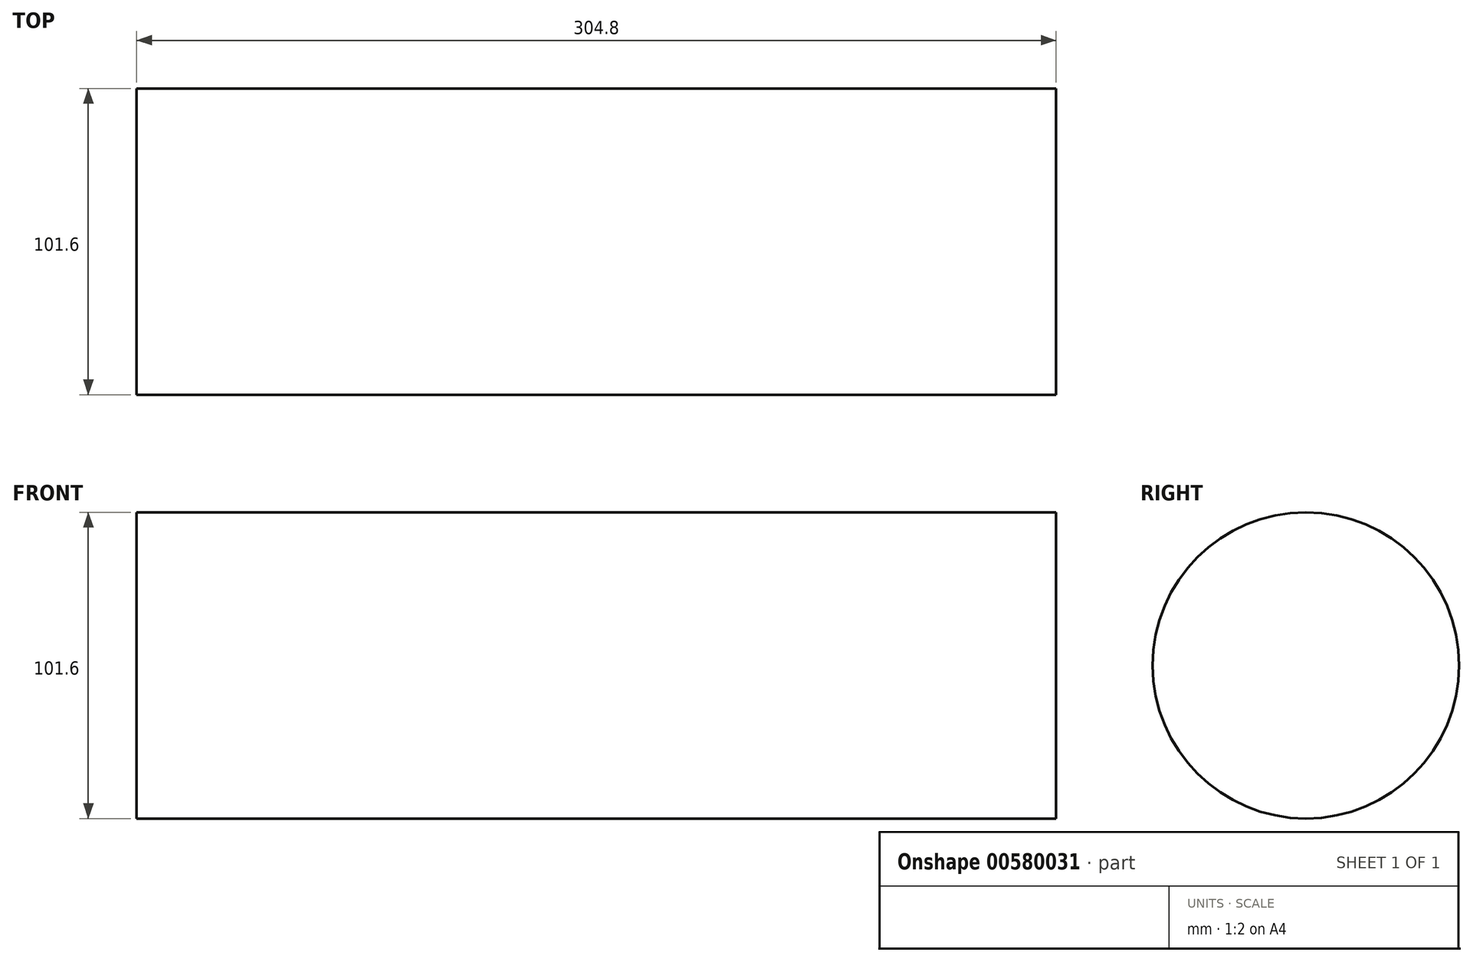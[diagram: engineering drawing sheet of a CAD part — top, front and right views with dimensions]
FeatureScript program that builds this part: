
annotation { "Feature Type Name" : "Feature", "Feature Type Description" : "" }
export const myFeature = defineFeature(function(context is Context, id is Id, definition is map)
    precondition{}
    {
        {
            var Q0;
            Q0=qCreatedBy(makeId("Right.planeOp"),FACE);
            var sketch = newSketch(context, id + "F0", { "sketchPlane" : qUnion([Q0])});
            skCircle(sketch, "E0", {"center": v(0, 0) * mm, "radius": 50.8 * mm});
            skSolve(sketch);
        }
        {
            var Q0;
            Q0 = qSketchRegion(id + "F0", true);
            extrude(context, id + "F1", {"entities" : qUnion([Q0]), "oppositeDirection" : true, "depth" : 304.8 * mm, "offsetDistance" : 25.4 * mm});
        }
    });
